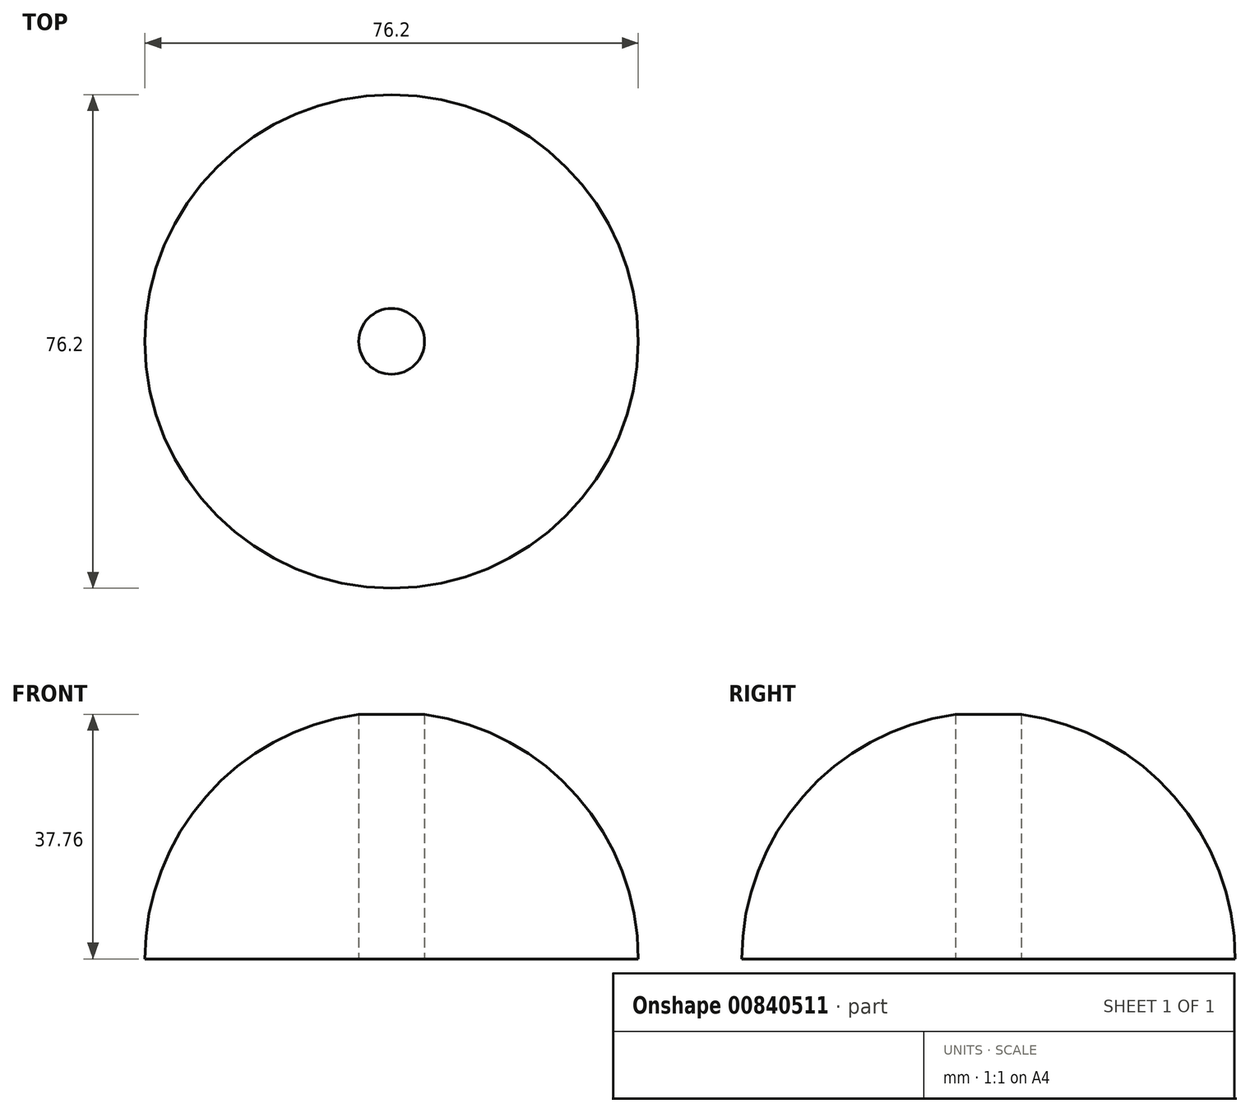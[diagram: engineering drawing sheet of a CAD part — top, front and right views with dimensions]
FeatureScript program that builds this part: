
annotation { "Feature Type Name" : "Feature", "Feature Type Description" : "" }
export const myFeature = defineFeature(function(context is Context, id is Id, definition is map)
    precondition{}
    {
        {
            var Q0;
            Q0=qCreatedBy(makeId("Top.planeOp"),FACE);
            var sketch = newSketch(context, id + "F0", { "sketchPlane" : qUnion([Q0])});
            skLineSegment(sketch, "E0", {"start": v(0, 0) * mm, "end": v(0, 76.2) * mm});
            skArc(sketch, "E1", {"start": v(0, 0) * mm, "mid": v(38.1, 38.1) * mm, "end": v(0, 76.2) * mm});
            skSolve(sketch);
        }
        {
            var Q0;
            Q0=makeQuery(id+"F0.imprint","IMPRINT",FACE,{"disambiguationData":[TD([[makeQuery(id+"F0.imprint","IMPRINT",EDGE,{"derivedFrom":sQuery(id+"F0.wireOp",EDGE,"E0")}),-1.0]])]});
            var Q1;
            Q1=sQuery(id+"F0.wireOp",EDGE,"E0");
            revolve(context, id + "F1", {"surfaceOperationType" : NewSurfaceOperationType.NEW, "entities" : qUnion([Q0]), "axis" : qUnion([Q1]), "revolveType" : RevolveType.ONE_DIRECTION, "oppositeDirection" : true, "angle" : 180 * degree});
        }
        {
            var Q0;
            Q0=makeQuery(id+"F1.opRevolve","CAP_FACE",FACE,{"disambiguationData":[OSD([sQuery(id+"F0.wireOp",EDGE,"E0"),sQuery(id+"F0.wireOp",EDGE,"E1")])],"isStart":true});
            var sketch = newSketch(context, id + "F2", { "sketchPlane" : qUnion([Q0])});
            skPoint(sketch, "E2", {"position": v(0, -38.1) * mm});
            skCircle(sketch, "E3", {"center": v(0, -38.1) * mm, "radius": 5.08 * mm});
            skSolve(sketch);
        }
        {
            var Q0;
            Q0=makeQuery(id+"F2.imprint","IMPRINT",FACE,{"disambiguationData":[TD([[makeQuery(id+"F2.imprint","IMPRINT",EDGE,{"derivedFrom":sQuery(id+"F2.wireOp",EDGE,"E3")}),1.0]])]});
            extrude(context, id + "F3", {"entities" : qUnion([Q0]), "operationType" : NewBodyOperationType.REMOVE, "oppositeDirection" : true, "depth" : 38.1 * mm, "offsetDistance" : 25.4 * mm});
        }
    });
